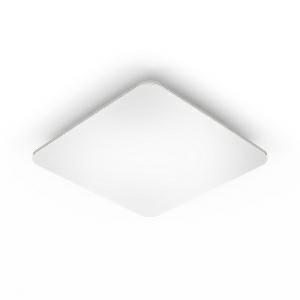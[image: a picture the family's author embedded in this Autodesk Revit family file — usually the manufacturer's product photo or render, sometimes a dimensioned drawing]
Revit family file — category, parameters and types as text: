
# Revit family: rs_pro_led_q1_007102
name_source: partatom
category: Leuchten
revit_build: Autodesk Revit 2016 (Build: 20190508_0715(x64)
units: mm (PartAtom-declared; Revit-internal decimal feet)

## family parameters
Basisbauteil = Fläche
Beim Laden mit Abzugskörper schneiden = Nein
Bemaßung runder Anschluss = Durchmesser verwenden
Gemeinsam genutzt = Nein
Lichtquelle = Nein
Raumberechnungspunkt = Nein
Teiletyp = Normal

## types (1)
- RS PRO LED Q1 (1 x , 2920 lm, 4000 K)
    Beschreibung = Dimensions (L x W x H): 56 x 331 x 331 mm; Mains power supply: 220 – 240 V / 50 – 60 Hz; Sensor Technology: High frequency; Transmitter power: < 1 mW; HF-system: 5,8 GHz; Output: 26 W; Interconnection: Yes; Type of interconnection: Master/master, Master/slave; Luminous flux: 2920 lm; Colour temperature: 4000 K; Colour variation LED: SDCM3; Colour Rendering Index CRI: 80-89; With lamp: Yes, STEINEL LED system; Lamp: LED cannot be replaced; LED life expectancy (max. °C): 50000 h; Drop in luminous flux in accordance with LM80: L70B10; Base: without; LED cooling system: Passive Thermo Control; With motion detector: Yes; Detection: also through glass, wood and stud walls; Detection angle: 360 °; Angle of aperture: 160 °; Capability of masking out individual segments: Yes; Electronic scalability: Yes; Mechanical scalability: No; Reach, radial: Ø 8 m (50 m²); Reach, tangential: Ø 8 m (50 m²); Main light adjustable: 50 - 100 %; Continuous light: selectable; Photo-cell controller: Yes; Twilight setting: 2 – 2000 lx; Time setting: 5 sec – 15 min; Basic light level function: Yes; Basic light level function time: 10/30 min, all night; Functions: Group parameterisation, Manual ON / ON-OFF, Master/slave override, Neighbouring-group function; Soft light start: Yes; Impact resistance: IK03; IP-rating: IP20; Protection class: II; Ambient temperature: -10 – 50 °C; Housing material: Aluminium; Cover material: Plastic, opal; Manufacturer's Warranty: 5 years; Settings via: DIP switches, Potentiometers, Remote control, Smart Remote; With remote control: No; Version: Neutral white silver; PU1, EAN: 4007841007102
    CIE Flux Codes = 46 77 95 100 100
    Color Rendering = 80-89
    Color Temperature = 4000 K
    Frequency = 50 Hz, 60 Hz
    Height = 331 mm
    Hersteller = Steinel
    Lamp Light Flux = 2920 lm
    Lamp count = 1
    Lampe = 1 x
    Length = 56 mm  [stored 0.183727 ft]
    Luminous efficacy = 112 lm/W
    ModVariant = Nein
    Modell = 007102
    Mounting Type = Surface mounted
    Number of Poles = 1
    OnlyDefault = Ja
    Power Factor = 1
    Product Name = RS PRO LED Q1
    Product group = Sensor-switched indoor light
    ProductGroupID = 30
    Protection Class = Protection class II
    Protection Degree = IP 20
    RlxData = <blob elided: 27893 chars, md5=7049ddee>
    Scheinlast = 26 VA
    Socket = socket
    Standby Power = 0 W
    System Light Flux = 2920 lm
    System Power = 26 W
    Typenbild = produkt1_007102.jpg
    Typenkommentare = Product without accessories
    URL = http://relux.com
    VarID = ---
    Voltage = 0 V
    Vorgabe-Ansicht = 1800 mm
    Weight = 0.00 kg
    Width = 331 mm

note: [stored X ft] marks values corroborated as IEEE doubles in the binary element streams (Revit-internal decimal feet)

## geometry (parser evidence)
native form markers: Blend x4, Sweep x8
no freeform markers — native parametric forms only
